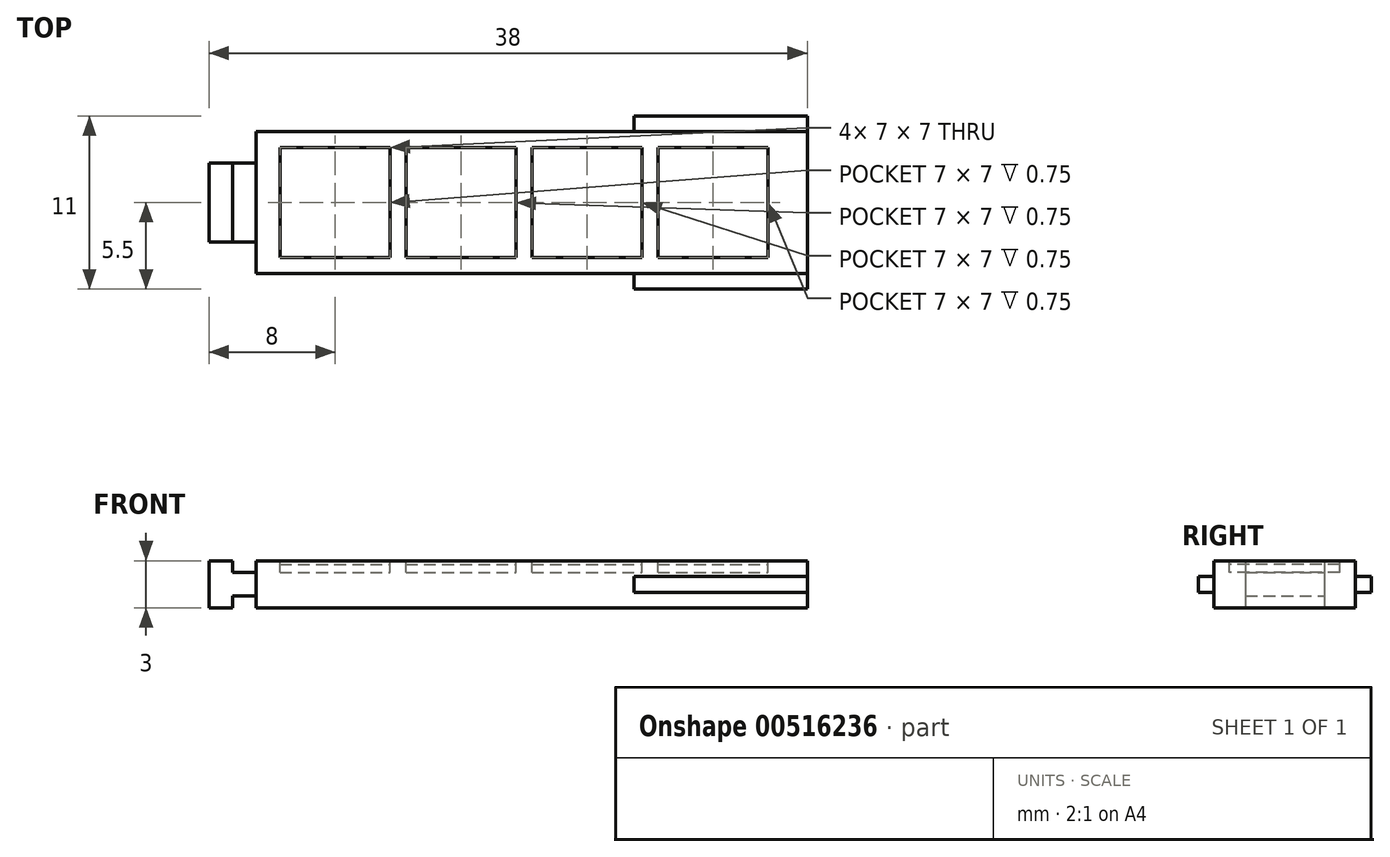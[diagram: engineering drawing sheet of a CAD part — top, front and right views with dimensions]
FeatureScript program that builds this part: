
annotation { "Feature Type Name" : "Feature", "Feature Type Description" : "" }
export const myFeature = defineFeature(function(context is Context, id is Id, definition is map)
    precondition{}
    {
        {
            var Q0;
            Q0=qCreatedBy(makeId("Front.planeOp"),FACE);
            var sketch = newSketch(context, id + "F0", { "sketchPlane" : qUnion([Q0])});
            skLineSegment(sketch, "E0.bottom", {"start": v(0, 3) * mm, "end": v(35, 3) * mm});
            skLineSegment(sketch, "E0.top", {"start": v(0, 0) * mm, "end": v(35, 0) * mm});
            skLineSegment(sketch, "E0.left", {"start": v(0, 3) * mm, "end": v(0, 0) * mm});
            skLineSegment(sketch, "E0.right", {"start": v(35, 3) * mm, "end": v(35, 0) * mm});
            skLineSegment(sketch, "E1", {"start": v(-13.71, 0) * mm, "end": v(-1.5, 0) * mm, "construction": true});
            skLineSegment(sketch, "E2", {"start": v(0, 1.6) * mm, "end": v(0, 6.8) * mm, "construction": true});
            skLineSegment(sketch, "E3", {"start": v(0, 1.5) * mm, "end": v(1.06, 0.44) * mm, "construction": true});
            skPoint(sketch, "E4.MirrorCS.start.orphan", {"position": v(-1.06, 0.44) * mm});
            skLineSegment(sketch, "E5.trimOffspring", {"start": v(0, 0) * mm, "end": v(15.8, 0) * mm, "construction": true});
            skPoint(sketch, "E6.end.orphan", {"position": v(1.5, 0) * mm});
            skLineSegment(sketch, "E7", {"start": v(-1.82, 1.5) * mm, "end": v(2.2, 1.5) * mm, "construction": true});
            skPoint(sketch, "E7.endSnap0", {"position": v(0, 1.5) * mm});
            skLineSegment(sketch, "E8.bottom", {"start": v(-3, 3) * mm, "end": v(-1.5, 3) * mm});
            skLineSegment(sketch, "E8.top", {"start": v(-3, 0) * mm, "end": v(-1.5, 0) * mm});
            skLineSegment(sketch, "E8.left", {"start": v(-3, 3) * mm, "end": v(-3, 0) * mm});
            skLineSegment(sketch, "E8.right", {"start": v(-1.5, 3) * mm, "end": v(-1.5, 0) * mm});
            skLineSegment(sketch, "E9", {"start": v(-3, 3) * mm, "end": v(0, 3) * mm, "construction": true});
            skLineSegment(sketch, "E10.bottom", {"start": v(-1.5, 2.25) * mm, "end": v(0, 2.25) * mm});
            skLineSegment(sketch, "E10.top", {"start": v(-1.5, 0.75) * mm, "end": v(0, 0.75) * mm});
            skLineSegment(sketch, "E10.left", {"start": v(-1.5, 2.25) * mm, "end": v(-1.5, 0.75) * mm});
            skLineSegment(sketch, "E10.right", {"start": v(0, 2.25) * mm, "end": v(0, 0.75) * mm});
            skSolve(sketch);
        }
        {
            var Q0;
            {var subQ3=sQuery(id+"F0.wireOp",EDGE,"E0.bottom");Q0=makeQuery(id+"F0.imprint","IMPRINT",FACE,{"disambiguationData":[TD([[makeQuery(id+"F0.imprint","IMPRINT",EDGE,{"derivedFrom":subQ3}),-1.0]])]});}
            extrude(context, id + "F1", {"entities" : qUnion([Q0]), "endBound" : BoundingType.SYMMETRIC, "depth" : (7 + 1 * 2) * mm, "offsetDistance" : 25 * mm});
        }
        {
            var Q0;
            Q0=makeQuery(id+"F1.opExtrude","SWEPT_FACE",FACE,{"disambiguationData":[OSD([sQuery(id+"F0.wireOp",EDGE,"E0.bottom")])]});
            var sketch = newSketch(context, id + "F2", { "sketchPlane" : qUnion([Q0])});
            skLineSegment(sketch, "E11.bottom", {"start": v(25.5, 3.5) * mm, "end": v(32.5, 3.5) * mm});
            skLineSegment(sketch, "E11.top", {"start": v(25.5, -3.5) * mm, "end": v(32.5, -3.5) * mm});
            skLineSegment(sketch, "E11.left", {"start": v(25.5, 3.5) * mm, "end": v(25.5, -3.5) * mm});
            skLineSegment(sketch, "E11.right", {"start": v(32.5, 3.5) * mm, "end": v(32.5, -3.5) * mm});
            skLineSegment(sketch, "E12.0", {"start": v(-13.71, 0) * mm, "end": v(-1.5, 0) * mm, "construction": true});
            skLineSegment(sketch, "E13.1.0.0", {"start": v(17.5, 3.5) * mm, "end": v(24.5, 3.5) * mm});
            skLineSegment(sketch, "E13.1.0.1", {"start": v(17.5, 3.5) * mm, "end": v(17.5, -3.5) * mm});
            skLineSegment(sketch, "E13.1.0.2", {"start": v(17.5, -3.5) * mm, "end": v(24.5, -3.5) * mm});
            skLineSegment(sketch, "E13.1.0.3", {"start": v(24.5, 3.5) * mm, "end": v(24.5, -3.5) * mm});
            skLineSegment(sketch, "E13.2.0.0", {"start": v(9.5, 3.5) * mm, "end": v(16.5, 3.5) * mm});
            skLineSegment(sketch, "E13.2.0.1", {"start": v(9.5, 3.5) * mm, "end": v(9.5, -3.5) * mm});
            skLineSegment(sketch, "E13.2.0.2", {"start": v(9.5, -3.5) * mm, "end": v(16.5, -3.5) * mm});
            skLineSegment(sketch, "E13.2.0.3", {"start": v(16.5, 3.5) * mm, "end": v(16.5, -3.5) * mm});
            skLineSegment(sketch, "E13.3.0.0", {"start": v(1.5, 3.5) * mm, "end": v(8.5, 3.5) * mm});
            skLineSegment(sketch, "E13.3.0.1", {"start": v(1.5, 3.5) * mm, "end": v(1.5, -3.5) * mm});
            skLineSegment(sketch, "E13.3.0.2", {"start": v(1.5, -3.5) * mm, "end": v(8.5, -3.5) * mm});
            skLineSegment(sketch, "E13.3.0.3", {"start": v(8.5, 3.5) * mm, "end": v(8.5, -3.5) * mm});
            skLineSegment(sketch, "E13.direction1", {"start": v(25.5, 3.5) * mm, "end": v(17.5, 3.5) * mm, "construction": true});
            skSolve(sketch);
        }
        {
            var Q0;
            Q0=makeQuery(id+"F2.imprint","IMPRINT",FACE,{"disambiguationData":[TD([[makeQuery(id+"F2.imprint","IMPRINT",EDGE,{"derivedFrom":sQuery(id+"F2.wireOp",EDGE,"E11.bottom")}),-1.0]])]});
            var Q1;
            Q1=makeQuery(id+"F2.imprint","IMPRINT",FACE,{"disambiguationData":[TD([[makeQuery(id+"F2.imprint","IMPRINT",EDGE,{"derivedFrom":sQuery(id+"F2.wireOp",EDGE,"E13.1.0.0")}),-1.0]])]});
            var Q2;
            Q2=makeQuery(id+"F2.imprint","IMPRINT",FACE,{"disambiguationData":[TD([[makeQuery(id+"F2.imprint","IMPRINT",EDGE,{"derivedFrom":sQuery(id+"F2.wireOp",EDGE,"E13.2.0.0")}),-1.0]])]});
            var Q3;
            Q3=makeQuery(id+"F2.imprint","IMPRINT",FACE,{"disambiguationData":[TD([[makeQuery(id+"F2.imprint","IMPRINT",EDGE,{"derivedFrom":sQuery(id+"F2.wireOp",EDGE,"E13.3.0.0")}),-1.0]])]});
            extrude(context, id + "F3", {"entities" : qUnion([Q0, Q1, Q2, Q3]), "operationType" : NewBodyOperationType.REMOVE, "oppositeDirection" : true, "depth" : .75 * mm, "offsetDistance" : 25 * mm});
        }
        {
            var Q0;
            Q0=makeQuery(id+"F2.imprint","IMPRINT",FACE,{"disambiguationData":[TD([[makeQuery(id+"F2.imprint","IMPRINT",EDGE,{"derivedFrom":sQuery(id+"F2.wireOp",EDGE,"E13.3.0.0")}),-1.0]])]});
            var Q1;
            Q1=makeQuery(id+"F2.imprint","IMPRINT",FACE,{"disambiguationData":[TD([[makeQuery(id+"F2.imprint","IMPRINT",EDGE,{"derivedFrom":sQuery(id+"F2.wireOp",EDGE,"E13.2.0.0")}),-1.0]])]});
            var Q2;
            Q2=makeQuery(id+"F2.imprint","IMPRINT",FACE,{"disambiguationData":[TD([[makeQuery(id+"F2.imprint","IMPRINT",EDGE,{"derivedFrom":sQuery(id+"F2.wireOp",EDGE,"E13.1.0.0")}),-1.0]])]});
            var Q3;
            Q3=makeQuery(id+"F2.imprint","IMPRINT",FACE,{"disambiguationData":[TD([[makeQuery(id+"F2.imprint","IMPRINT",EDGE,{"derivedFrom":sQuery(id+"F2.wireOp",EDGE,"E11.bottom")}),-1.0]])]});
            extrude(context, id + "F4", {"entities" : qUnion([Q0, Q1, Q2, Q3]), "oppositeDirection" : true, "depth" : .5 * mm, "offsetDistance" : 25 * mm});
        }
        {
            var Q0;
            Q0=makeQuery(id+"F1.opExtrude","CAP_FACE",FACE,{"disambiguationData":[OSD([sQuery(id+"F0.wireOp",EDGE,"E0.bottom"),sQuery(id+"F0.wireOp",EDGE,"E0.top"),sQuery(id+"F0.wireOp",EDGE,"E0.left"),sQuery(id+"F0.wireOp",EDGE,"E0.right")])],"isStart":false});
            var sketch = newSketch(context, id + "F5", { "sketchPlane" : qUnion([Q0])});
            skPoint(sketch, "E14.orphan", {"position": v(34.2, 12.17) * mm});
            skLineSegment(sketch, "E15.right", {"start": v(35, 2) * mm, "end": v(35, 1) * mm});
            skLineSegment(sketch, "E16.bottom", {"start": v(24, 2) * mm, "end": v(34, 2) * mm});
            skLineSegment(sketch, "E16.top", {"start": v(24, 1) * mm, "end": v(34, 1) * mm});
            skLineSegment(sketch, "E16.left", {"start": v(24, 2) * mm, "end": v(24, 1) * mm});
            skLineSegment(sketch, "E17", {"start": v(16.6, 1.5) * mm, "end": v(35, 1.5) * mm, "construction": true});
            skPoint(sketch, "E17.startSnap0", {"position": v(24, 1.5) * mm});
            skLineSegment(sketch, "E18", {"start": v(34, 1) * mm, "end": v(35, 1) * mm});
            skLineSegment(sketch, "E19", {"start": v(34, 2) * mm, "end": v(35, 2) * mm});
            skPoint(sketch, "E20.orphan", {"position": v(35, 3) * mm});
            skPoint(sketch, "E15.top.end.orphan", {"position": v(35, 0) * mm});
            skLineSegment(sketch, "E21.0", {"start": v(35, 0) * mm, "end": v(35, 3) * mm});
            skSolve(sketch);
        }
        {
            var Q0;
            Q0=makeQuery(id+"F5.imprint","IMPRINT",FACE,{"disambiguationData":[TD([[makeQuery(id+"F5.imprint","IMPRINT",EDGE,{"derivedFrom":sQuery(id+"F5.wireOp",EDGE,"E16.bottom")}),-1.0]])]});
            extrude(context, id + "F6", {"entities" : qUnion([Q0]), "operationType" : NewBodyOperationType.ADD, "depth" : 1 * mm, "offsetDistance" : 25 * mm});
        }
        {
            var Q0;
            Q0=makeQuery(id+"F1.opExtrude","SWEPT_BODY",BODY,{"disambiguationData":[OSD([sQuery(id+"F0.wireOp",EDGE,"E0.bottom"),sQuery(id+"F0.wireOp",EDGE,"E0.top"),sQuery(id+"F0.wireOp",EDGE,"E0.left"),sQuery(id+"F0.wireOp",EDGE,"E0.right")])]});
            var Q1;
            Q1=qCreatedBy(makeId("Front.planeOp"),FACE);
            mirror(context, id + "F7", {"entities" : qUnion([Q0]), "mirrorPlane" : qUnion([Q1])});
        }
        {
            var Q0;
            {var subQ1=sQuery(id+"F0.wireOp",EDGE,"E8.bottom");Q0=makeQuery(id+"F0.imprint","IMPRINT",FACE,{"disambiguationData":[TD([[makeQuery(id+"F0.imprint","IMPRINT",EDGE,{"derivedFrom":subQ1}),-1.0]])]});}
            var Q1;
            Q1=makeQuery(id+"F0.imprint","IMPRINT",FACE,{"disambiguationData":[TD([[makeQuery(id+"F0.imprint","IMPRINT",EDGE,{"derivedFrom":sQuery(id+"F0.wireOp",EDGE,"E10.bottom")}),-1.0]])]});
            extrude(context, id + "F8", {"entities" : qUnion([Q0, Q1]), "endBound" : BoundingType.SYMMETRIC, "depth" : 5 * mm, "offsetDistance" : 25 * mm});
        }
        {
            var Q0;
            Q0=makeQuery(id+"F4.opExtrude","SWEPT_BODY",BODY,{"disambiguationData":[OSD([sQuery(id+"F2.wireOp",EDGE,"E13.1.0.0"),sQuery(id+"F2.wireOp",EDGE,"E13.1.0.1"),sQuery(id+"F2.wireOp",EDGE,"E13.1.0.2"),sQuery(id+"F2.wireOp",EDGE,"E13.1.0.3")])]});
            var Q1;
            Q1=makeQuery(id+"F4.opExtrude","SWEPT_BODY",BODY,{"disambiguationData":[OSD([sQuery(id+"F2.wireOp",EDGE,"E13.2.0.0"),sQuery(id+"F2.wireOp",EDGE,"E13.2.0.1"),sQuery(id+"F2.wireOp",EDGE,"E13.2.0.2"),sQuery(id+"F2.wireOp",EDGE,"E13.2.0.3")])]});
            var Q2;
            Q2=makeQuery(id+"F4.opExtrude","SWEPT_BODY",BODY,{"disambiguationData":[OSD([sQuery(id+"F2.wireOp",EDGE,"E13.3.0.0"),sQuery(id+"F2.wireOp",EDGE,"E13.3.0.1"),sQuery(id+"F2.wireOp",EDGE,"E13.3.0.2"),sQuery(id+"F2.wireOp",EDGE,"E13.3.0.3")])]});
            var Q3;
            Q3=makeQuery(id+"F4.opExtrude","SWEPT_BODY",BODY,{"disambiguationData":[OSD([sQuery(id+"F2.wireOp",EDGE,"E11.bottom"),sQuery(id+"F2.wireOp",EDGE,"E11.top"),sQuery(id+"F2.wireOp",EDGE,"E11.left"),sQuery(id+"F2.wireOp",EDGE,"E11.right")])]});
            var Q4;
            Q4=sQuery(id+"F0.wireOp",EDGE,"E2");
            var Q5;
            Q5=sQuery(id+"F0.wireOp",EDGE,"E2");
            transform(context, id + "F9", {"entities" : qUnion([Q0, Q1, Q2, Q3]), "transformType" : TransformType.TRANSLATION_DISTANCE, "transformDirection" : qUnion([Q5]), "distance" : .25 * mm, "oppositeDirection" : true, "makeCopy" : false});
        }
    });
